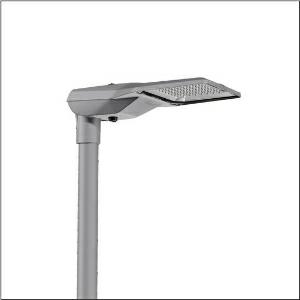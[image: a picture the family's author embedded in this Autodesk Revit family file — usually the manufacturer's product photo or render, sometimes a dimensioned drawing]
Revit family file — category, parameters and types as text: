
# Revit family: streetlight_sl_21_iq_midi___st1_0a_5xe3d31y08mb_3ca9
name_source: partatom
category: Lighting Fixtures
units: mm (PartAtom-declared; Revit-internal decimal feet)

## family parameters
Cut with Voids When Loaded = No
Host = Face
Light Source = No
Part Type = Normal
Room Calculation Point = No
Round Connector Dimension = Use Diameter
Shared = No

## types (1)
- --- (1 x LED, 18340 lm, 129.3 W, 3000K)
    Apparent Load = 129 VA
    CIE Flux Codes = 37 72 97 100 100
    Color Rendering = 70
    Color Temperature = 3000K
    Default Elevation = 1800 mm
    Description = Streetlight SL 21 iQ midi, mast luminaire, primary light control with lens, of PMMA, primary optical cover: cover, of toughened safety glass, transparent, light distribution: ST1.0a, light emission: direct distribution, primary light characteristic: asymmetric, installation type: post-top, side-entry, LED, High Power LED, rated luminous flux: 18.340lm, luminous efficacy: 142lm/W, light colour: 730, colour temperature: 3000K, control gear: iQ-Street Remote, D4i with power reduction, control: pre-setting: logarithmic dimming characteristic, Street-Remote, Auto-Match, Temp-Guard, Lumen-Switch, Night-Set, Smart-Wire, Light-Fading, Desk-Remote (wireless, voltage-free reading and setting of iQ features in the workshop via application-optimized NFC function/RFID function), optimised constant luminous flux control (CLO 2.0), mains connection: 230..240V, AC, 50/60Hz, start of lifetime: 129W, end of service life: 142W, reduction: 56W, luminaire housing, of diecast aluminium, powder-coated, Siteco® metallic grey (DB 702S), corrosivity category C5 mid according to DIN EN ISO 12944, please order mast flange separately, inclination adjustable: 0°, 5°, 10°, 15°, sealing non-destructively replaceable, multi-level sealing system, length: 644mm, width: 335mm, height: 110mm, mast flange for spigot size: 42mm (side-entry): 5XC10008XM4, 60/48mm (side-entry/post-top): 5XC10108XM2, 76/60mm (side-entry/post-top): 5XC10108XM1, mounting height: 4..8m, Smart Interface below and above, protection rating (complete): IP66, insulation class (complete): insulation class II (safety insulation), certification: CE, ENEC, ENEC+, VDE, impact resistance: IK10, permissible operating ambient temperature for outdoor applications: -40..+50°C, standard-compliant lighting for roads and squares, packaging unit: 1 piece

Light Distribution: ST1.0a
    Height = 111 mm
    Lamp = 1 x LED
    Lamp Light Flux = 18340 lm
    Lamp Power = 129.3 W
    Lamp count = 1
    Length = 644 mm
    Luminous efficacy = 142 lm/W
    Manufacturer = Siteco
    ModVariant = No
    Model = 5XE3D31Y08MB
    Number of Poles = 1
    OnlyDefault = Yes
    Power Factor = 1
    Product Name = Streetlight SL 21 iQ midi | ST1.0a
    Product group = mast luminaire | pylon top
    ProductGroupID = 6100
    Protection Class = Protection class II
    Protection Degree = IP 66
    RLX_Detail_Level = 1
    RLX_Emergency_Light_Flux = 0 lm
    RLX_Emergency_Type = 0
    RLX_Emergency_Type_DB = No
    RlxData = <blob elided: 90821 chars, md5=b643e6f0>
    Socket = socket
    Standby Power = 0 W
    System Light Flux = 18340 lm
    System Power = 129 W
    Type Comments = factory setting: luminous flux: 100 % | dim-lin: 254 | 672 mA
    Type Image = l_1004304.jpg
    URL = http://relux.com
    VarID = @adj_136007
    Voltage = 0 V
    Weight = 0.00 kg
    Width = 336 mm

## geometry (parser evidence)
native form markers: Blend x4, Sweep x12
no freeform markers — native parametric forms only
